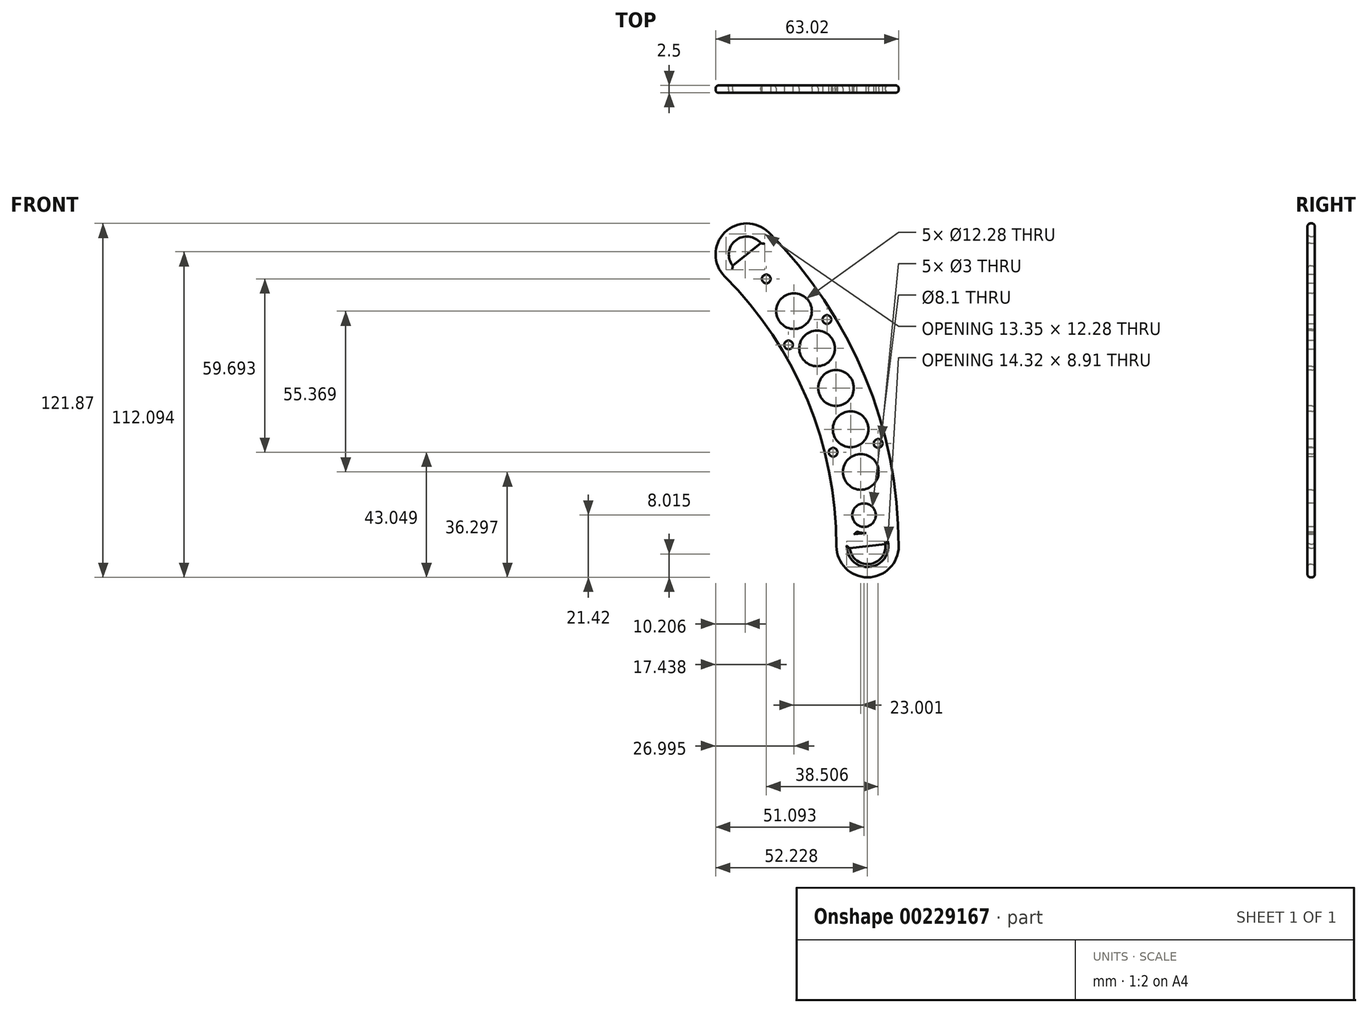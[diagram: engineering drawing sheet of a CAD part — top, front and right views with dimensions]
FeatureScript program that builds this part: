
annotation { "Feature Type Name" : "Feature", "Feature Type Description" : "" }
export const myFeature = defineFeature(function(context is Context, id is Id, definition is map)
    precondition{}
    {
        {
            var Q0;
            Q0=qCreatedBy(makeId("Front.planeOp"),FACE);
            var sketch = newSketch(context, id + "F0", { "sketchPlane" : qUnion([Q0])});
            skCircle(sketch, "E0", {"center": v(0, 0) * mm, "radius": 152.8 * mm});
            skCircle(sketch, "E1", {"center": v(0, 0) * mm, "radius": 131.4 * mm});
            skLineSegment(sketch, "E2", {"start": v(0, 0) * mm, "end": v(152.8, 0) * mm, "construction": true});
            skLineSegment(sketch, "E3", {"start": v(0, 0) * mm, "end": v(108.04, 108.04) * mm, "construction": true});
            skPoint(sketch, "E4", {"position": v(92.9, 92.9) * mm});
            skPoint(sketch, "E5", {"position": v(108.04, 108.04) * mm});
            skPoint(sketch, "E6", {"position": v(131.4, 0) * mm});
            skPoint(sketch, "E7", {"position": v(152.8, 0) * mm});
            skCircle(sketch, "E8", {"center": v(100.47, 100.47) * mm, "radius": 10.7 * mm});
            skCircle(sketch, "E9", {"center": v(142.1, 0) * mm, "radius": 10.7 * mm});
            skLineSegment(sketch, "E10", {"start": v(142.1, 0) * mm, "end": v(148.23, 0.7) * mm});
            skLineSegment(sketch, "E11", {"start": v(142.1, 0) * mm, "end": v(135.94, -0.7) * mm});
            skLineSegment(sketch, "E12", {"start": v(148.23, 0.7) * mm, "end": v(144.58, 32.71) * mm});
            skLineSegment(sketch, "E13", {"start": v(135.94, -0.7) * mm, "end": v(132.3, 31.31) * mm});
            skLineSegment(sketch, "E14", {"start": v(132.3, 31.31) * mm, "end": v(144.58, 32.71) * mm});
            skLineSegment(sketch, "E15", {"start": v(100.47, 100.47) * mm, "end": v(105.3, 104.33) * mm});
            skLineSegment(sketch, "E16", {"start": v(100.47, 100.47) * mm, "end": v(95.64, 96.62) * mm});
            skLineSegment(sketch, "E17", {"start": v(120.53, 75.25) * mm, "end": v(125.41, 79.16) * mm});
            skLineSegment(sketch, "E18", {"start": v(120.53, 75.25) * mm, "end": v(115.75, 71.44) * mm});
            skLineSegment(sketch, "E19", {"start": v(105.3, 104.33) * mm, "end": v(125.41, 79.16) * mm});
            skLineSegment(sketch, "E20", {"start": v(95.64, 96.62) * mm, "end": v(115.75, 71.44) * mm});
            skLineSegment(sketch, "E21", {"start": v(135.42, 3.88) * mm, "end": v(147.7, 5.28) * mm});
            skLineSegment(sketch, "E22", {"start": v(132.82, 26.73) * mm, "end": v(145.1, 28.13) * mm});
            skLineSegment(sketch, "E23", {"start": v(112.88, 75.04) * mm, "end": v(122.53, 82.76) * mm});
            skLineSegment(sketch, "E24", {"start": v(98.52, 93.01) * mm, "end": v(108.18, 100.73) * mm});
            skCircle(sketch, "E25", {"center": v(0, 0) * mm, "radius": 148.23 * mm, "construction": true});
            skCircle(sketch, "E26", {"center": v(0, 0) * mm, "radius": 135.95 * mm, "construction": true});
            skCircle(sketch, "E27", {"center": v(141.82, 2.29) * mm, "radius": 1 * mm});
            skCircle(sketch, "E28", {"center": v(138.7, 29.72) * mm, "radius": 1 * mm});
            skCircle(sketch, "E29", {"center": v(140.86, 10.72) * mm, "radius": 6.18 * mm});
            skLineSegment(sketch, "E30", {"start": v(122.53, 82.76) * mm, "end": v(115.75, 71.44) * mm, "construction": true});
            skLineSegment(sketch, "E31", {"start": v(112.88, 75.04) * mm, "end": v(125.41, 79.16) * mm, "construction": true});
            skCircle(sketch, "E32", {"center": v(101.91, 98.67) * mm, "radius": 1 * mm});
            skCircle(sketch, "E33", {"center": v(119.14, 77.1) * mm, "radius": 1 * mm});
            skCircle(sketch, "E34", {"center": v(107.2, 92.04) * mm, "radius": 6.18 * mm});
            skLineSegment(sketch, "E35", {"start": v(132.82, 26.73) * mm, "end": v(144.58, 32.71) * mm, "construction": true});
            skLineSegment(sketch, "E36", {"start": v(145.1, 28.13) * mm, "end": v(132.3, 31.31) * mm, "construction": true});
            skCircle(sketch, "E37", {"center": v(100.47, 100.47) * mm, "radius": 6.18 * mm});
            skCircle(sketch, "E38", {"center": v(142.1, 0) * mm, "radius": 6.19 * mm});
            skLineSegment(sketch, "E39", {"start": v(135.42, 3.88) * mm, "end": v(148.23, 0.7) * mm, "construction": true});
            skLineSegment(sketch, "E40", {"start": v(135.94, -0.7) * mm, "end": v(147.7, 5.28) * mm, "construction": true});
            skLineSegment(sketch, "E41", {"start": v(148.23, 0.7) * mm, "end": v(148.24, 0.7) * mm});
            skSolve(sketch);
        }
        {
            var Q0;
            {var subQ16=sQuery(id+"F0.wireOp",EDGE,"E18");Q0=makeQuery(id+"F0.imprint","IMPRINT",FACE,{"disambiguationData":[TD([[makeQuery(id+"F0.imprint","IMPRINT",EDGE,{"derivedFrom":subQ16}),1.0]])]});}
            var Q1;
            {var subQ14=sQuery(id+"F0.wireOp",EDGE,"E17");Q1=makeQuery(id+"F0.imprint","IMPRINT",FACE,{"disambiguationData":[TD([[makeQuery(id+"F0.imprint","IMPRINT",EDGE,{"derivedFrom":subQ14}),-1.0]])]});}
            var Q2;
            {var subQ3=sQuery(id+"F0.wireOp",EDGE,"oQQra7B9-EMDj-B2YQ-GpEd-beqhVWcHA2Qh");var subQ5=sQuery(id+"F0.wireOp",EDGE,"E22");var subQ9=makeQuery(id+"F0.imprint","INTERSECT",VERTEX,{"derivedFrom":[subQ3,subQ5]});Q2=makeQuery(id+"F0.imprint","IMPRINT",FACE,{"disambiguationData":[TD([[makeQuery(id+"F0.imprint","IMPRINT",EDGE,{"disambiguationData":[TD([[subQ9,-1.0]])],"derivedFrom":subQ3}),-1.0]])]});}
            var Q3;
            {var subQ3=sQuery(id+"F0.wireOp",EDGE,"oQQra7B9-EMDj-B2YQ-GpEd-beqhVWcHA2Qh");var subQ5=sQuery(id+"F0.wireOp",EDGE,"E22");var subQ9=makeQuery(id+"F0.imprint","INTERSECT",VERTEX,{"derivedFrom":[subQ3,subQ5]});Q3=makeQuery(id+"F0.imprint","IMPRINT",FACE,{"disambiguationData":[TD([[makeQuery(id+"F0.imprint","IMPRINT",EDGE,{"disambiguationData":[TD([[subQ9,-1.0]])],"derivedFrom":subQ3}),1.0]])]});}
            var Q4;
            {var subQ5=sQuery(id+"F0.wireOp",EDGE,"E9");var subQ8=makeQuery(id+"F0.imprint","INTERSECT",VERTEX,{"derivedFrom":[sQuery(id+"F0.wireOp",EDGE,"E1"),subQ5]});Q4=makeQuery(id+"F0.imprint","IMPRINT",FACE,{"disambiguationData":[TD([[makeQuery(id+"F0.imprint","IMPRINT",EDGE,{"disambiguationData":[TD([[subQ8,1.0]])],"derivedFrom":subQ5}),1.0]])]});}
            var Q5;
            {var subQ1=sQuery(id+"F0.wireOp",EDGE,"E9");var subQ5=makeQuery(id+"F0.imprint","INTERSECT",VERTEX,{"derivedFrom":[sQuery(id+"F0.wireOp",EDGE,"E0"),subQ1]});Q5=makeQuery(id+"F0.imprint","IMPRINT",FACE,{"disambiguationData":[TD([[makeQuery(id+"F0.imprint","IMPRINT",EDGE,{"disambiguationData":[TD([[subQ5,-1.0]])],"derivedFrom":subQ1}),1.0]])]});}
            var Q6;
            {var subQ1=sQuery(id+"F0.wireOp",EDGE,"E13");var subQ3=sQuery(id+"F0.wireOp",EDGE,"E21");var subQ4=makeQuery(id+"F0.imprint","INTERSECT",VERTEX,{"derivedFrom":[subQ1,subQ3]});Q6=makeQuery(id+"F0.imprint","IMPRINT",FACE,{"disambiguationData":[TD([[makeQuery(id+"F0.imprint","IMPRINT",EDGE,{"disambiguationData":[TD([[subQ4,-1.0]])],"derivedFrom":subQ3}),-1.0]])]});}
            var Q7;
            {var subQ1=sQuery(id+"F0.wireOp",EDGE,"E12");var subQ3=sQuery(id+"F0.wireOp",EDGE,"E21");var subQ4=makeQuery(id+"F0.imprint","INTERSECT",VERTEX,{"derivedFrom":[subQ1,subQ3]});Q7=makeQuery(id+"F0.imprint","IMPRINT",FACE,{"disambiguationData":[TD([[makeQuery(id+"F0.imprint","IMPRINT",EDGE,{"disambiguationData":[TD([[subQ4,1.0]])],"derivedFrom":subQ3}),-1.0]])]});}
            var Q8;
            {var subQ4=sQuery(id+"F0.wireOp",EDGE,"E8");var subQ5=makeQuery(id+"F0.imprint","INTERSECT",VERTEX,{"derivedFrom":[sQuery(id+"F0.wireOp",EDGE,"E0"),subQ4]});Q8=makeQuery(id+"F0.imprint","IMPRINT",FACE,{"disambiguationData":[TD([[makeQuery(id+"F0.imprint","IMPRINT",EDGE,{"disambiguationData":[TD([[subQ5,-1.0]])],"derivedFrom":subQ4}),1.0]])]});}
            var Q9;
            {var subQ5=sQuery(id+"F0.wireOp",EDGE,"E8");var subQ9=makeQuery(id+"F0.imprint","INTERSECT",VERTEX,{"derivedFrom":[sQuery(id+"F0.wireOp",EDGE,"E1"),subQ5]});Q9=makeQuery(id+"F0.imprint","IMPRINT",FACE,{"disambiguationData":[TD([[makeQuery(id+"F0.imprint","IMPRINT",EDGE,{"disambiguationData":[TD([[subQ9,1.0]])],"derivedFrom":subQ5}),1.0]])]});}
            var Q10;
            {var subQ1=sQuery(id+"F0.wireOp",EDGE,"E20");var subQ3=sQuery(id+"F0.wireOp",EDGE,"E24");var subQ4=makeQuery(id+"F0.imprint","INTERSECT",VERTEX,{"derivedFrom":[subQ1,subQ3]});Q10=makeQuery(id+"F0.imprint","IMPRINT",FACE,{"disambiguationData":[TD([[makeQuery(id+"F0.imprint","IMPRINT",EDGE,{"disambiguationData":[TD([[subQ4,-1.0]])],"derivedFrom":subQ3}),1.0]])]});}
            var Q11;
            {var subQ4=sQuery(id+"F0.wireOp",EDGE,"E16");Q11=makeQuery(id+"F0.imprint","IMPRINT",FACE,{"disambiguationData":[TD([[makeQuery(id+"F0.imprint","IMPRINT",EDGE,{"derivedFrom":subQ4}),1.0]])]});}
            var Q12;
            {var subQ0=sQuery(id+"F0.wireOp",EDGE,"E15");Q12=makeQuery(id+"F0.imprint","IMPRINT",FACE,{"disambiguationData":[TD([[makeQuery(id+"F0.imprint","IMPRINT",EDGE,{"derivedFrom":subQ0}),-1.0]])]});}
            var Q13;
            {var subQ1=sQuery(id+"F0.wireOp",EDGE,"E19");var subQ3=sQuery(id+"F0.wireOp",EDGE,"E24");var subQ4=makeQuery(id+"F0.imprint","INTERSECT",VERTEX,{"derivedFrom":[subQ1,subQ3]});Q13=makeQuery(id+"F0.imprint","IMPRINT",FACE,{"disambiguationData":[TD([[makeQuery(id+"F0.imprint","IMPRINT",EDGE,{"disambiguationData":[TD([[subQ4,1.0]])],"derivedFrom":subQ3}),1.0]])]});}
            var Q14;
            {var subQ1=sQuery(id+"F0.wireOp",EDGE,"E18");Q14=makeQuery(id+"F0.imprint","IMPRINT",FACE,{"disambiguationData":[TD([[makeQuery(id+"F0.imprint","IMPRINT",EDGE,{"derivedFrom":subQ1}),-1.0]])]});}
            var Q15;
            {var subQ1=sQuery(id+"F0.wireOp",EDGE,"E17");Q15=makeQuery(id+"F0.imprint","IMPRINT",FACE,{"disambiguationData":[TD([[makeQuery(id+"F0.imprint","IMPRINT",EDGE,{"derivedFrom":subQ1}),1.0]])]});}
            var Q16;
            {var subQ0=sQuery(id+"F0.wireOp",EDGE,"E14");Q16=makeQuery(id+"F0.imprint","IMPRINT",FACE,{"disambiguationData":[TD([[makeQuery(id+"F0.imprint","IMPRINT",EDGE,{"derivedFrom":subQ0}),-1.0]])]});}
            var Q17;
            {var subQ5=sQuery(id+"F0.wireOp",EDGE,"E10");Q17=makeQuery(id+"F0.imprint","IMPRINT",FACE,{"disambiguationData":[TD([[makeQuery(id+"F0.imprint","IMPRINT",EDGE,{"derivedFrom":subQ5}),1.0]])]});}
            var Q18;
            Q18=makeQuery(id+"F0.imprint","IMPRINT",FACE,{"disambiguationData":[TD([[makeQuery(id+"F0.imprint","IMPRINT",EDGE,{"derivedFrom":sQuery(id+"F0.wireOp",EDGE,"E27")}),-1.0]])]});
            var Q19;
            {var subQ0=sQuery(id+"F0.wireOp",EDGE,"E41");Q19=makeQuery(id+"F0.imprint","IMPRINT",FACE,{"disambiguationData":[TD([[makeQuery(id+"F0.imprint","IMPRINT",EDGE,{"derivedFrom":subQ0}),1.0]])]});}
            extrude(context, id + "F1", {"entities" : qUnion([Q0, Q1, Q2, Q3, Q4, Q5, Q6, Q7, Q8, Q9, Q10, Q11, Q12, Q13, Q14, Q15, Q16, Q17, Q18, Q19]), "depth" : 2.5 * mm});
        }
        {
            var Q0;
            Q0=makeQuery(id+"F1.opExtrude","CAP_FACE",FACE,{"disambiguationData":[OSD([sQuery(id+"F0.wireOp",EDGE,"E0"),sQuery(id+"F0.wireOp",EDGE,"E1"),sQuery(id+"F0.wireOp",EDGE,"E8"),sQuery(id+"F0.wireOp",EDGE,"E9"),sQuery(id+"F0.wireOp",EDGE,"E10"),sQuery(id+"F0.wireOp",EDGE,"E11"),sQuery(id+"F0.wireOp",EDGE,"E12"),sQuery(id+"F0.wireOp",EDGE,"E13"),sQuery(id+"F0.wireOp",EDGE,"E15"),sQuery(id+"F0.wireOp",EDGE,"E16"),sQuery(id+"F0.wireOp",EDGE,"E19"),sQuery(id+"F0.wireOp",EDGE,"E20"),sQuery(id+"F0.wireOp",EDGE,"E21"),sQuery(id+"F0.wireOp",EDGE,"E22"),sQuery(id+"F0.wireOp",EDGE,"E23"),sQuery(id+"F0.wireOp",EDGE,"E24"),sQuery(id+"F0.wireOp",EDGE,"E27"),sQuery(id+"F0.wireOp",EDGE,"E28"),sQuery(id+"F0.wireOp",EDGE,"E32"),sQuery(id+"F0.wireOp",EDGE,"E33"),sQuery(id+"F0.wireOp",EDGE,"E37"),sQuery(id+"F0.wireOp",EDGE,"E38")])],"isStart":false});
            var sketch = newSketch(context, id + "F2", { "sketchPlane" : qUnion([Q0])});
            skCircle(sketch, "E42", {"center": v(136.26, 40.28) * mm, "radius": 6.14 * mm});
            skCircle(sketch, "E43", {"center": v(124.7, 68.12) * mm, "radius": 6.14 * mm});
            skCircle(sketch, "E44", {"center": v(131.22, 54.5) * mm, "radius": 6.14 * mm});
            skCircle(sketch, "E45", {"center": v(0, 0) * mm, "radius": 142.1 * mm, "construction": true});
            skLineSegment(sketch, "E46", {"start": v(0, 0) * mm, "end": v(136.26, 40.28) * mm, "construction": true});
            skLineSegment(sketch, "E47", {"start": v(0, 0) * mm, "end": v(131.22, 54.5) * mm, "construction": true});
            skLineSegment(sketch, "E48", {"start": v(0, 0) * mm, "end": v(124.7, 68.12) * mm, "construction": true});
            skCircle(sketch, "E49", {"center": v(0, 0) * mm, "radius": 152.8 * mm, "construction": true});
            skCircle(sketch, "E50", {"center": v(0, 0) * mm, "radius": 131.4 * mm, "construction": true});
            skCircle(sketch, "E51", {"center": v(0, 0) * mm, "radius": 135.95 * mm, "construction": true});
            skCircle(sketch, "E52", {"center": v(0, 0) * mm, "radius": 148.23 * mm, "construction": true});
            skLineSegment(sketch, "E53", {"start": v(112.88, 75.04) * mm, "end": v(119.3, 65.18) * mm, "construction": true});
            skLineSegment(sketch, "E54", {"start": v(119.3, 65.18) * mm, "end": v(118, 79.14) * mm, "construction": true});
            skLineSegment(sketch, "E55", {"start": v(118, 79.14) * mm, "end": v(130.08, 71.07) * mm, "construction": true});
            skLineSegment(sketch, "E56", {"start": v(130.08, 71.07) * mm, "end": v(122.53, 82.76) * mm, "construction": true});
            skLineSegment(sketch, "E57", {"start": v(122.53, 82.76) * mm, "end": v(118, 79.14) * mm});
            skLineSegment(sketch, "E58", {"start": v(112.88, 75.04) * mm, "end": v(118, 79.14) * mm});
            skLineSegment(sketch, "E59", {"start": v(126.3, 76.91) * mm, "end": v(130.43, 79.57) * mm, "construction": true});
            skCircle(sketch, "E60", {"center": v(128.1, 78.07) * mm, "radius": 1 * mm});
            skLineSegment(sketch, "E61", {"start": v(130.37, 38.54) * mm, "end": v(132.82, 26.73) * mm});
            skLineSegment(sketch, "E62", {"start": v(145.1, 28.13) * mm, "end": v(142.22, 41.78) * mm});
            skLineSegment(sketch, "E63", {"start": v(131.6, 32.64) * mm, "end": v(127.49, 31.79) * mm});
            skLineSegment(sketch, "E64", {"start": v(143.66, 34.96) * mm, "end": v(148.5, 35.98) * mm});
            skCircle(sketch, "E65", {"center": v(130.21, 32.35) * mm, "radius": 1 * mm});
            skCircle(sketch, "E66", {"center": v(145.71, 35.4) * mm, "radius": 1 * mm});
            skLineSegment(sketch, "E67", {"start": v(116.1, 70.11) * mm, "end": v(112.55, 67.8) * mm, "construction": true});
            skCircle(sketch, "E68", {"center": v(114.87, 69.32) * mm, "radius": 1 * mm});
            skLineSegment(sketch, "E69", {"start": v(0, 0) * mm, "end": v(116.76, 80.97) * mm, "construction": true});
            skLineSegment(sketch, "E70", {"start": v(0, 0) * mm, "end": v(139.77, 25.6) * mm, "construction": true});
            skCircle(sketch, "E71", {"center": v(139.77, 25.6) * mm, "radius": 6.14 * mm});
            skCircle(sketch, "E72", {"center": v(116.76, 80.97) * mm, "radius": 6.14 * mm});
            skSolve(sketch);
        }
        {
            var Q0;
            Q0=makeQuery(id+"F2.imprint","IMPRINT",FACE,{"disambiguationData":[TD([[makeQuery(id+"F2.imprint","IMPRINT",EDGE,{"derivedFrom":sQuery(id+"F2.wireOp",EDGE,"E43")}),1.0]])]});
            var Q1;
            Q1=makeQuery(id+"F2.imprint","IMPRINT",FACE,{"disambiguationData":[TD([[makeQuery(id+"F2.imprint","IMPRINT",EDGE,{"derivedFrom":sQuery(id+"F2.wireOp",EDGE,"E44")}),1.0]])]});
            var Q2;
            Q2=makeQuery(id+"F2.imprint","IMPRINT",FACE,{"disambiguationData":[TD([[makeQuery(id+"F2.imprint","IMPRINT",EDGE,{"derivedFrom":sQuery(id+"F2.wireOp",EDGE,"E42")}),1.0]])]});
            var Q3;
            {var subQ0=sQuery(id+"F2.wireOp",EDGE,"E56");var subQ1=sQuery(id+"F2.wireOp",EDGE,"E43");var subQ2=makeQuery(id+"F2.imprint","INTERSECT",VERTEX,{"derivedFrom":[subQ1,subQ0]});Q3=makeQuery(id+"F2.imprint","IMPRINT",FACE,{"disambiguationData":[TD([[makeQuery(id+"F2.imprint","IMPRINT",EDGE,{"disambiguationData":[TD([[subQ2,-1.0]])],"derivedFrom":subQ1}),1.0]])]});}
            var Q4;
            {var subQ0=sQuery(id+"F2.wireOp",EDGE,"E54");var subQ1=sQuery(id+"F2.wireOp",EDGE,"E43");var subQ3=makeQuery(id+"F2.imprint","INTERSECT",VERTEX,{"derivedFrom":[subQ1,subQ0]});Q4=makeQuery(id+"F2.imprint","IMPRINT",FACE,{"disambiguationData":[TD([[makeQuery(id+"F2.imprint","IMPRINT",EDGE,{"disambiguationData":[TD([[subQ3,-1.0]])],"derivedFrom":subQ1}),1.0]])]});}
            var Q5;
            Q5=makeQuery(id+"F2.imprint","IMPRINT",FACE,{"disambiguationData":[TD([[makeQuery(id+"F2.imprint","IMPRINT",EDGE,{"derivedFrom":sQuery(id+"F2.wireOp",EDGE,"6Q9i7ZKX-M5Zn-dDvE-S5ua-DKoOSJd4rO0q")}),1.0]])]});
            var Q6;
            Q6=makeQuery(id+"F2.imprint","IMPRINT",FACE,{"disambiguationData":[TD([[makeQuery(id+"F2.imprint","IMPRINT",EDGE,{"derivedFrom":sQuery(id+"F2.wireOp",EDGE,"E60")}),1.0]])]});
            var Q7;
            Q7=makeQuery(id+"F2.imprint","IMPRINT",FACE,{"disambiguationData":[TD([[makeQuery(id+"F2.imprint","IMPRINT",EDGE,{"derivedFrom":sQuery(id+"F2.wireOp",EDGE,"E68")}),1.0]])]});
            var Q8;
            {var subQ0=sQuery(id+"F2.wireOp",EDGE,"E66");var subQ1=sQuery(id+"F2.wireOp",EDGE,"E64");var subQ2=makeQuery(id+"F2.imprint","INTERSECT",VERTEX,{"disambiguationData":[OD(0.0)],"derivedFrom":[subQ1,subQ0]});Q8=makeQuery(id+"F2.imprint","IMPRINT",FACE,{"disambiguationData":[TD([[makeQuery(id+"F2.imprint","IMPRINT",EDGE,{"disambiguationData":[TD([[subQ2,-1.0]])],"derivedFrom":subQ1}),1.0]])]});}
            var Q9;
            {var subQ0=sQuery(id+"F2.wireOp",EDGE,"E66");var subQ1=sQuery(id+"F2.wireOp",EDGE,"E64");var subQ2=makeQuery(id+"F2.imprint","INTERSECT",VERTEX,{"disambiguationData":[OD(0.0)],"derivedFrom":[subQ1,subQ0]});Q9=makeQuery(id+"F2.imprint","IMPRINT",FACE,{"disambiguationData":[TD([[makeQuery(id+"F2.imprint","IMPRINT",EDGE,{"disambiguationData":[TD([[subQ2,-1.0]])],"derivedFrom":subQ1}),-1.0]])]});}
            var Q10;
            {var subQ0=sQuery(id+"F2.wireOp",EDGE,"E65");var subQ1=sQuery(id+"F2.wireOp",EDGE,"E63");var subQ2=makeQuery(id+"F2.imprint","INTERSECT",VERTEX,{"disambiguationData":[OD(0.0)],"derivedFrom":[subQ1,subQ0]});Q10=makeQuery(id+"F2.imprint","IMPRINT",FACE,{"disambiguationData":[TD([[makeQuery(id+"F2.imprint","IMPRINT",EDGE,{"disambiguationData":[TD([[subQ2,-1.0]])],"derivedFrom":subQ1}),1.0]])]});}
            var Q11;
            {var subQ0=sQuery(id+"F2.wireOp",EDGE,"E65");var subQ1=sQuery(id+"F2.wireOp",EDGE,"E63");var subQ2=makeQuery(id+"F2.imprint","INTERSECT",VERTEX,{"disambiguationData":[OD(0.0)],"derivedFrom":[subQ1,subQ0]});Q11=makeQuery(id+"F2.imprint","IMPRINT",FACE,{"disambiguationData":[TD([[makeQuery(id+"F2.imprint","IMPRINT",EDGE,{"disambiguationData":[TD([[subQ2,-1.0]])],"derivedFrom":subQ1}),-1.0]])]});}
            extrude(context, id + "F3", {"entities" : qUnion([Q0, Q1, Q2, Q3, Q4, Q5, Q6, Q7, Q8, Q9, Q10, Q11]), "operationType" : NewBodyOperationType.REMOVE, "oppositeDirection" : true, "depth" : 25 * mm});
        }
        {
            var Q0;
            {var subQ1=sQuery(id+"F0.wireOp",EDGE,"E9");var subQ6=sQuery(id+"F0.wireOp",EDGE,"E12");var subQ8=makeQuery(id+"F0.imprint","INTERSECT",VERTEX,{"derivedFrom":[subQ1,subQ6]});Q0=makeQuery(id+"F0.imprint","IMPRINT",FACE,{"disambiguationData":[TD([[makeQuery(id+"F0.imprint","IMPRINT",EDGE,{"disambiguationData":[TD([[subQ8,-1.0]])],"derivedFrom":subQ1}),1.0]])]});}
            var Q1;
            {var subQ0=sQuery(id+"F0.wireOp",EDGE,"E29");var subQ1=sQuery(id+"F0.wireOp",EDGE,"E9");var subQ2=makeQuery(id+"F0.imprint","INTERSECT",VERTEX,{"disambiguationData":[OD(0.0)],"derivedFrom":[subQ1,subQ0]});Q1=makeQuery(id+"F0.imprint","IMPRINT",FACE,{"disambiguationData":[TD([[makeQuery(id+"F0.imprint","IMPRINT",EDGE,{"disambiguationData":[TD([[subQ2,-1.0]])],"derivedFrom":subQ1}),-1.0]])]});}
            var Q2;
            {var subQ0=sQuery(id+"F0.wireOp",EDGE,"E29");var subQ1=sQuery(id+"F0.wireOp",EDGE,"E9");var subQ2=makeQuery(id+"F0.imprint","INTERSECT",VERTEX,{"disambiguationData":[OD(0.0)],"derivedFrom":[subQ1,subQ0]});Q2=makeQuery(id+"F0.imprint","IMPRINT",FACE,{"disambiguationData":[TD([[makeQuery(id+"F0.imprint","IMPRINT",EDGE,{"disambiguationData":[TD([[subQ2,-1.0]])],"derivedFrom":subQ1}),1.0]])]});}
            var Q3;
            {var subQ0=sQuery(id+"F0.wireOp",EDGE,"E29");var subQ1=makeQuery(id+"F0.imprint","INTERSECT",VERTEX,{"derivedFrom":[sQuery(id+"F0.wireOp",EDGE,"E21"),subQ0]});Q3=makeQuery(id+"F0.imprint","IMPRINT",FACE,{"disambiguationData":[TD([[makeQuery(id+"F0.imprint","IMPRINT",EDGE,{"disambiguationData":[TD([[subQ1,1.0]])],"derivedFrom":subQ0}),1.0]])]});}
            var Q4;
            {var subQ0=sQuery(id+"F0.wireOp",EDGE,"E29");var subQ1=sQuery(id+"F0.wireOp",EDGE,"E9");var subQ2=makeQuery(id+"F0.imprint","INTERSECT",VERTEX,{"disambiguationData":[OD(1.0)],"derivedFrom":[subQ1,subQ0]});Q4=makeQuery(id+"F0.imprint","IMPRINT",FACE,{"disambiguationData":[TD([[makeQuery(id+"F0.imprint","IMPRINT",EDGE,{"disambiguationData":[TD([[subQ2,-1.0]])],"derivedFrom":subQ1}),1.0]])]});}
            var Q5;
            {var subQ0=sQuery(id+"F0.wireOp",EDGE,"E38");var subQ1=sQuery(id+"F0.wireOp",EDGE,"E21");var subQ2=makeQuery(id+"F0.imprint","INTERSECT",VERTEX,{"disambiguationData":[OD(0.0)],"derivedFrom":[subQ1,subQ0]});Q5=makeQuery(id+"F0.imprint","IMPRINT",FACE,{"disambiguationData":[TD([[makeQuery(id+"F0.imprint","IMPRINT",EDGE,{"disambiguationData":[TD([[subQ2,-1.0]])],"derivedFrom":subQ1}),1.0]])]});}
            var Q6;
            {var subQ0=sQuery(id+"F0.wireOp",EDGE,"E29");var subQ1=sQuery(id+"F0.wireOp",EDGE,"E21");var subQ2=makeQuery(id+"F0.imprint","INTERSECT",VERTEX,{"derivedFrom":[subQ1,subQ0]});Q6=makeQuery(id+"F0.imprint","IMPRINT",FACE,{"disambiguationData":[TD([[makeQuery(id+"F0.imprint","IMPRINT",EDGE,{"disambiguationData":[TD([[subQ2,-1.0]])],"derivedFrom":subQ1}),1.0]])]});}
            var Q7;
            {var subQ0=sQuery(id+"F0.wireOp",EDGE,"E22");Q7=makeQuery(id+"F0.imprint","IMPRINT",FACE,{"disambiguationData":[TD([[makeQuery(id+"F0.imprint","IMPRINT",EDGE,{"derivedFrom":subQ0}),-1.0]])]});}
            var Q8;
            {var subQ0=sQuery(id+"F0.wireOp",EDGE,"E12");var subQ1=sQuery(id+"F0.wireOp",EDGE,"E9");var subQ2=makeQuery(id+"F0.imprint","INTERSECT",VERTEX,{"derivedFrom":[subQ1,subQ0]});Q8=makeQuery(id+"F0.imprint","IMPRINT",FACE,{"disambiguationData":[TD([[makeQuery(id+"F0.imprint","IMPRINT",EDGE,{"disambiguationData":[TD([[subQ2,-1.0]])],"derivedFrom":subQ1}),-1.0]])]});}
            var Q9;
            {var subQ0=sQuery(id+"F0.wireOp",EDGE,"E29");var subQ1=sQuery(id+"F0.wireOp",EDGE,"E9");var subQ2=makeQuery(id+"F0.imprint","INTERSECT",VERTEX,{"disambiguationData":[OD(1.0)],"derivedFrom":[subQ1,subQ0]});Q9=makeQuery(id+"F0.imprint","IMPRINT",FACE,{"disambiguationData":[TD([[makeQuery(id+"F0.imprint","IMPRINT",EDGE,{"disambiguationData":[TD([[subQ2,-1.0]])],"derivedFrom":subQ1}),-1.0]])]});}
            var Q10;
            {var subQ0=sQuery(id+"F0.wireOp",EDGE,"E23");Q10=makeQuery(id+"F0.imprint","IMPRINT",FACE,{"disambiguationData":[TD([[makeQuery(id+"F0.imprint","IMPRINT",EDGE,{"derivedFrom":subQ0}),1.0]])]});}
            var Q11;
            {var subQ0=sQuery(id+"F0.wireOp",EDGE,"E34");var subQ1=sQuery(id+"F0.wireOp",EDGE,"E8");var subQ2=makeQuery(id+"F0.imprint","INTERSECT",VERTEX,{"disambiguationData":[OD(0.0)],"derivedFrom":[subQ1,subQ0]});Q11=makeQuery(id+"F0.imprint","IMPRINT",FACE,{"disambiguationData":[TD([[makeQuery(id+"F0.imprint","IMPRINT",EDGE,{"disambiguationData":[TD([[subQ2,-1.0]])],"derivedFrom":subQ1}),-1.0]])]});}
            var Q12;
            {var subQ0=sQuery(id+"F0.wireOp",EDGE,"E34");var subQ1=sQuery(id+"F0.wireOp",EDGE,"E8");var subQ2=makeQuery(id+"F0.imprint","INTERSECT",VERTEX,{"disambiguationData":[OD(0.0)],"derivedFrom":[subQ1,subQ0]});Q12=makeQuery(id+"F0.imprint","IMPRINT",FACE,{"disambiguationData":[TD([[makeQuery(id+"F0.imprint","IMPRINT",EDGE,{"disambiguationData":[TD([[subQ2,-1.0]])],"derivedFrom":subQ1}),1.0]])]});}
            var Q13;
            {var subQ0=sQuery(id+"F0.wireOp",EDGE,"E34");var subQ1=sQuery(id+"F0.wireOp",EDGE,"E8");var subQ2=makeQuery(id+"F0.imprint","INTERSECT",VERTEX,{"disambiguationData":[OD(1.0)],"derivedFrom":[subQ1,subQ0]});Q13=makeQuery(id+"F0.imprint","IMPRINT",FACE,{"disambiguationData":[TD([[makeQuery(id+"F0.imprint","IMPRINT",EDGE,{"disambiguationData":[TD([[subQ2,-1.0]])],"derivedFrom":subQ1}),1.0]])]});}
            var Q14;
            {var subQ0=sQuery(id+"F0.wireOp",EDGE,"E34");var subQ1=sQuery(id+"F0.wireOp",EDGE,"E24");var subQ2=makeQuery(id+"F0.imprint","INTERSECT",VERTEX,{"derivedFrom":[subQ1,subQ0]});Q14=makeQuery(id+"F0.imprint","IMPRINT",FACE,{"disambiguationData":[TD([[makeQuery(id+"F0.imprint","IMPRINT",EDGE,{"disambiguationData":[TD([[subQ2,-1.0]])],"derivedFrom":subQ1}),-1.0]])]});}
            var Q15;
            {var subQ0=sQuery(id+"F0.wireOp",EDGE,"E34");var subQ1=makeQuery(id+"F0.imprint","INTERSECT",VERTEX,{"derivedFrom":[sQuery(id+"F0.wireOp",EDGE,"E24"),subQ0]});Q15=makeQuery(id+"F0.imprint","IMPRINT",FACE,{"disambiguationData":[TD([[makeQuery(id+"F0.imprint","IMPRINT",EDGE,{"disambiguationData":[TD([[subQ1,1.0]])],"derivedFrom":subQ0}),1.0]])]});}
            var Q16;
            {var subQ0=sQuery(id+"F0.wireOp",EDGE,"E37");var subQ1=sQuery(id+"F0.wireOp",EDGE,"E24");var subQ2=makeQuery(id+"F0.imprint","INTERSECT",VERTEX,{"disambiguationData":[OD(0.0)],"derivedFrom":[subQ1,subQ0]});Q16=makeQuery(id+"F0.imprint","IMPRINT",FACE,{"disambiguationData":[TD([[makeQuery(id+"F0.imprint","IMPRINT",EDGE,{"disambiguationData":[TD([[subQ2,-1.0]])],"derivedFrom":subQ1}),-1.0]])]});}
            var Q17;
            {var subQ1=sQuery(id+"F0.wireOp",EDGE,"E8");var subQ6=sQuery(id+"F0.wireOp",EDGE,"E20");var subQ9=makeQuery(id+"F0.imprint","INTERSECT",VERTEX,{"derivedFrom":[subQ1,subQ6]});Q17=makeQuery(id+"F0.imprint","IMPRINT",FACE,{"disambiguationData":[TD([[makeQuery(id+"F0.imprint","IMPRINT",EDGE,{"disambiguationData":[TD([[subQ9,-1.0]])],"derivedFrom":subQ1}),1.0]])]});}
            var Q18;
            {var subQ0=sQuery(id+"F0.wireOp",EDGE,"E34");var subQ1=sQuery(id+"F0.wireOp",EDGE,"E8");var subQ2=makeQuery(id+"F0.imprint","INTERSECT",VERTEX,{"disambiguationData":[OD(1.0)],"derivedFrom":[subQ1,subQ0]});Q18=makeQuery(id+"F0.imprint","IMPRINT",FACE,{"disambiguationData":[TD([[makeQuery(id+"F0.imprint","IMPRINT",EDGE,{"disambiguationData":[TD([[subQ2,-1.0]])],"derivedFrom":subQ1}),-1.0]])]});}
            var Q19;
            {var subQ0=sQuery(id+"F0.wireOp",EDGE,"E20");var subQ1=sQuery(id+"F0.wireOp",EDGE,"E8");var subQ2=makeQuery(id+"F0.imprint","INTERSECT",VERTEX,{"derivedFrom":[subQ1,subQ0]});Q19=makeQuery(id+"F0.imprint","IMPRINT",FACE,{"disambiguationData":[TD([[makeQuery(id+"F0.imprint","IMPRINT",EDGE,{"disambiguationData":[TD([[subQ2,-1.0]])],"derivedFrom":subQ1}),-1.0]])]});}
            extrude(context, id + "F4", {"entities" : qUnion([Q0, Q1, Q2, Q3, Q4, Q5, Q6, Q7, Q8, Q9, Q10, Q11, Q12, Q13, Q14, Q15, Q16, Q17, Q18, Q19]), "operationType" : NewBodyOperationType.ADD, "depth" : 2.5 * mm});
        }
        {
            var Q0;
            {var subQ0=sQuery(id+"F0.wireOp",EDGE,"E24");var subQ1=sQuery(id+"F0.wireOp",EDGE,"E23");var subQ2=sQuery(id+"F0.wireOp",EDGE,"E20");var subQ3=sQuery(id+"F0.wireOp",EDGE,"E19");var subQ4=sQuery(id+"F0.wireOp",EDGE,"E22");var subQ5=sQuery(id+"F0.wireOp",EDGE,"E21");var subQ6=sQuery(id+"F0.wireOp",EDGE,"E13");var subQ7=sQuery(id+"F0.wireOp",EDGE,"E12");Q0=makeQuery(id+"F4.boolean.opBoolean","MERGE",FACE,{"derivedFrom":[makeQuery(id+"F1.opExtrude","CAP_FACE",FACE,{"disambiguationData":[OSD([sQuery(id+"F0.wireOp",EDGE,"E0"),sQuery(id+"F0.wireOp",EDGE,"E1"),sQuery(id+"F0.wireOp",EDGE,"E8"),sQuery(id+"F0.wireOp",EDGE,"E9"),sQuery(id+"F0.wireOp",EDGE,"E10"),sQuery(id+"F0.wireOp",EDGE,"E11"),subQ7,subQ6,sQuery(id+"F0.wireOp",EDGE,"E15"),sQuery(id+"F0.wireOp",EDGE,"E16"),subQ3,subQ2,subQ5,subQ4,subQ1,subQ0,sQuery(id+"F0.wireOp",EDGE,"E27"),sQuery(id+"F0.wireOp",EDGE,"E28"),sQuery(id+"F0.wireOp",EDGE,"E32"),sQuery(id+"F0.wireOp",EDGE,"E33"),sQuery(id+"F0.wireOp",EDGE,"E37"),sQuery(id+"F0.wireOp",EDGE,"E38")])],"isStart":false}),makeQuery(id+"F4.opExtrude","CAP_FACE",FACE,{"disambiguationData":[OSD([subQ7,subQ6,subQ5,subQ4])],"isStart":false}),makeQuery(id+"F4.opExtrude","CAP_FACE",FACE,{"disambiguationData":[OSD([subQ3,subQ2,subQ1,subQ0])],"isStart":false})]});}
            var sketch = newSketch(context, id + "F5", { "sketchPlane" : qUnion([Q0])});
            skCircle(sketch, "E73", {"center": v(140.86, 10.72) * mm, "radius": 4.05 * mm});
            skCircle(sketch, "E74", {"center": v(107.2, 92.04) * mm, "radius": 4.05 * mm});
            skSolve(sketch);
        }
        {
            var Q0;
            Q0 = qSketchRegion(id + "F5", true);
            extrude(context, id + "F6", {"entities" : qUnion([Q0]), "operationType" : NewBodyOperationType.REMOVE, "oppositeDirection" : true, "depth" : 25 * mm});
        }
        {
            var Q0;
            Q0=makeQuery(id+"F0.imprint","IMPRINT",FACE,{"disambiguationData":[TD([[makeQuery(id+"F0.imprint","IMPRINT",EDGE,{"derivedFrom":sQuery(id+"F0.wireOp",EDGE,"E32")}),1.0]])]});
            var Q1;
            Q1=makeQuery(id+"F0.imprint","IMPRINT",FACE,{"disambiguationData":[TD([[makeQuery(id+"F0.imprint","IMPRINT",EDGE,{"derivedFrom":sQuery(id+"F0.wireOp",EDGE,"E33")}),1.0]])]});
            var Q2;
            Q2=makeQuery(id+"F0.imprint","IMPRINT",FACE,{"disambiguationData":[TD([[makeQuery(id+"F0.imprint","IMPRINT",EDGE,{"derivedFrom":sQuery(id+"F0.wireOp",EDGE,"E28")}),1.0]])]});
            var Q3;
            Q3=makeQuery(id+"F0.imprint","IMPRINT",FACE,{"disambiguationData":[TD([[makeQuery(id+"F0.imprint","IMPRINT",EDGE,{"derivedFrom":sQuery(id+"F0.wireOp",EDGE,"E27")}),1.0]])]});
            extrude(context, id + "F7", {"entities" : qUnion([Q0, Q1, Q2, Q3]), "operationType" : NewBodyOperationType.ADD, "depth" : 2.5 * mm});
        }
        {
            var Q0;
            {var subQ0=sQuery(id+"F2.wireOp",EDGE,"E71");var subQ1=makeQuery(id+"F1.opExtrude","CAP_EDGE",EDGE,{"disambiguationData":[OSD([sQuery(id+"F0.wireOp",EDGE,"E22")])],"isStart":false});var subQ2=makeQuery(id+"F2.imprint","INTERSECT",VERTEX,{"derivedFrom":[subQ1,subQ0]});Q0=makeQuery(id+"F2.imprint","IMPRINT",FACE,{"disambiguationData":[TD([[makeQuery(id+"F2.imprint","IMPRINT",EDGE,{"disambiguationData":[TD([[subQ2,-1.0]])],"derivedFrom":subQ0}),1.0]])]});}
            var Q1;
            Q1=makeQuery(id+"F2.imprint","IMPRINT",FACE,{"disambiguationData":[TD([[makeQuery(id+"F2.imprint","IMPRINT",EDGE,{"derivedFrom":makeQuery(id+"F1.opExtrude","CAP_EDGE",EDGE,{"disambiguationData":[OSD([sQuery(id+"F0.wireOp",EDGE,"E28")])],"isStart":false})}),-1.0]])]});
            var Q2;
            Q2=makeQuery(id+"F2.imprint","IMPRINT",FACE,{"disambiguationData":[TD([[makeQuery(id+"F2.imprint","IMPRINT",EDGE,{"derivedFrom":makeQuery(id+"F1.opExtrude","CAP_EDGE",EDGE,{"disambiguationData":[OSD([sQuery(id+"F0.wireOp",EDGE,"E28")])],"isStart":false})}),1.0]])]});
            var Q3;
            {var subQ0=sQuery(id+"F2.wireOp",EDGE,"E62");var subQ3=sQuery(id+"F2.wireOp",EDGE,"E71");var subQ4=makeQuery(id+"F2.imprint","INTERSECT",VERTEX,{"derivedFrom":[subQ0,subQ3]});Q3=makeQuery(id+"F2.imprint","IMPRINT",FACE,{"disambiguationData":[TD([[makeQuery(id+"F2.imprint","IMPRINT",EDGE,{"disambiguationData":[TD([[subQ4,1.0]])],"derivedFrom":subQ3}),1.0]])]});}
            var Q4;
            {var subQ0=sQuery(id+"F2.wireOp",EDGE,"E57");Q4=makeQuery(id+"F2.imprint","IMPRINT",FACE,{"disambiguationData":[TD([[makeQuery(id+"F2.imprint","IMPRINT",EDGE,{"derivedFrom":subQ0}),1.0]])]});}
            var Q5;
            {var subQ5=sQuery(id+"F2.wireOp",EDGE,"E57");Q5=makeQuery(id+"F2.imprint","IMPRINT",FACE,{"disambiguationData":[TD([[makeQuery(id+"F2.imprint","IMPRINT",EDGE,{"derivedFrom":subQ5}),-1.0]])]});}
            var Q6;
            Q6=makeQuery(id+"F2.imprint","IMPRINT",FACE,{"disambiguationData":[TD([[makeQuery(id+"F2.imprint","IMPRINT",EDGE,{"derivedFrom":makeQuery(id+"F1.opExtrude","CAP_EDGE",EDGE,{"disambiguationData":[OSD([sQuery(id+"F0.wireOp",EDGE,"E33")])],"isStart":false})}),1.0]])]});
            extrude(context, id + "F8", {"entities" : qUnion([Q0, Q1, Q2, Q3, Q4, Q5, Q6]), "operationType" : NewBodyOperationType.REMOVE, "oppositeDirection" : true, "depth" : 25 * mm});
        }
        {
            var Q0;
            Q0=makeQuery(id+"F8.boolean.opBoolean","COPY",EDGE,{"derivedFrom":makeQuery(id+"F8.opExtrude","CAP_EDGE",EDGE,{"disambiguationData":[OSD([sQuery(id+"F2.wireOp",EDGE,"E72")])],"isStart":true})});
            var Q1;
            Q1=makeQuery(id+"F8.boolean.opBoolean","COPY",EDGE,{"derivedFrom":makeQuery(id+"F8.opExtrude","CAP_EDGE",EDGE,{"disambiguationData":[OSD([sQuery(id+"F2.wireOp",EDGE,"E71")])],"isStart":true})});
            var Q2;
            {var subQ0=sQuery(id+"F0.wireOp",EDGE,"E33");var subQ1=sQuery(id+"F0.wireOp",EDGE,"E32");var subQ2=sQuery(id+"F0.wireOp",EDGE,"E28");var subQ3=sQuery(id+"F0.wireOp",EDGE,"E27");var subQ4=sQuery(id+"F0.wireOp",EDGE,"E24");var subQ5=sQuery(id+"F0.wireOp",EDGE,"E23");var subQ6=sQuery(id+"F0.wireOp",EDGE,"E20");var subQ7=sQuery(id+"F0.wireOp",EDGE,"E19");var subQ8=sQuery(id+"F0.wireOp",EDGE,"E22");var subQ9=sQuery(id+"F0.wireOp",EDGE,"E21");var subQ10=sQuery(id+"F0.wireOp",EDGE,"E13");var subQ11=sQuery(id+"F0.wireOp",EDGE,"E12");Q2=makeQuery(id+"F8.boolean.opBoolean","INTERSECT",EDGE,{"derivedFrom":[makeQuery(id+"F7.boolean.opBoolean","MERGE",FACE,{"derivedFrom":[makeQuery(id+"F4.boolean.opBoolean","MERGE",FACE,{"derivedFrom":[makeQuery(id+"F1.opExtrude","CAP_FACE",FACE,{"disambiguationData":[OSD([sQuery(id+"F0.wireOp",EDGE,"E0"),sQuery(id+"F0.wireOp",EDGE,"E1"),sQuery(id+"F0.wireOp",EDGE,"E8"),sQuery(id+"F0.wireOp",EDGE,"E9"),sQuery(id+"F0.wireOp",EDGE,"E10"),sQuery(id+"F0.wireOp",EDGE,"E11"),subQ11,subQ10,sQuery(id+"F0.wireOp",EDGE,"E15"),sQuery(id+"F0.wireOp",EDGE,"E16"),subQ7,subQ6,subQ9,subQ8,subQ5,subQ4,subQ3,subQ2,subQ1,subQ0,sQuery(id+"F0.wireOp",EDGE,"E37"),sQuery(id+"F0.wireOp",EDGE,"E38")])],"isStart":true}),makeQuery(id+"F4.opExtrude","CAP_FACE",FACE,{"disambiguationData":[OSD([subQ11,subQ10,subQ9,subQ8])],"isStart":true}),makeQuery(id+"F4.opExtrude","CAP_FACE",FACE,{"disambiguationData":[OSD([subQ7,subQ6,subQ5,subQ4])],"isStart":true})]}),makeQuery(id+"F7.opExtrude","CAP_FACE",FACE,{"disambiguationData":[OSD([subQ3])],"isStart":true}),makeQuery(id+"F7.opExtrude","CAP_FACE",FACE,{"disambiguationData":[OSD([subQ2])],"isStart":true}),makeQuery(id+"F7.opExtrude","CAP_FACE",FACE,{"disambiguationData":[OSD([subQ1])],"isStart":true}),makeQuery(id+"F7.opExtrude","CAP_FACE",FACE,{"disambiguationData":[OSD([subQ0])],"isStart":true})]}),makeQuery(id+"F8.opExtrude","SWEPT_FACE",FACE,{"disambiguationData":[OSD([sQuery(id+"F2.wireOp",EDGE,"E71")])]})]});}
            var Q3;
            {var subQ0=sQuery(id+"F0.wireOp",EDGE,"E33");var subQ1=sQuery(id+"F0.wireOp",EDGE,"E32");var subQ2=sQuery(id+"F0.wireOp",EDGE,"E28");var subQ3=sQuery(id+"F0.wireOp",EDGE,"E27");var subQ4=sQuery(id+"F0.wireOp",EDGE,"E24");var subQ5=sQuery(id+"F0.wireOp",EDGE,"E23");var subQ6=sQuery(id+"F0.wireOp",EDGE,"E20");var subQ7=sQuery(id+"F0.wireOp",EDGE,"E19");var subQ8=sQuery(id+"F0.wireOp",EDGE,"E22");var subQ9=sQuery(id+"F0.wireOp",EDGE,"E21");var subQ10=sQuery(id+"F0.wireOp",EDGE,"E13");var subQ11=sQuery(id+"F0.wireOp",EDGE,"E12");Q3=makeQuery(id+"F8.boolean.opBoolean","INTERSECT",EDGE,{"derivedFrom":[makeQuery(id+"F7.boolean.opBoolean","MERGE",FACE,{"derivedFrom":[makeQuery(id+"F4.boolean.opBoolean","MERGE",FACE,{"derivedFrom":[makeQuery(id+"F1.opExtrude","CAP_FACE",FACE,{"disambiguationData":[OSD([sQuery(id+"F0.wireOp",EDGE,"E0"),sQuery(id+"F0.wireOp",EDGE,"E1"),sQuery(id+"F0.wireOp",EDGE,"E8"),sQuery(id+"F0.wireOp",EDGE,"E9"),sQuery(id+"F0.wireOp",EDGE,"E10"),sQuery(id+"F0.wireOp",EDGE,"E11"),subQ11,subQ10,sQuery(id+"F0.wireOp",EDGE,"E15"),sQuery(id+"F0.wireOp",EDGE,"E16"),subQ7,subQ6,subQ9,subQ8,subQ5,subQ4,subQ3,subQ2,subQ1,subQ0,sQuery(id+"F0.wireOp",EDGE,"E37"),sQuery(id+"F0.wireOp",EDGE,"E38")])],"isStart":true}),makeQuery(id+"F4.opExtrude","CAP_FACE",FACE,{"disambiguationData":[OSD([subQ11,subQ10,subQ9,subQ8])],"isStart":true}),makeQuery(id+"F4.opExtrude","CAP_FACE",FACE,{"disambiguationData":[OSD([subQ7,subQ6,subQ5,subQ4])],"isStart":true})]}),makeQuery(id+"F7.opExtrude","CAP_FACE",FACE,{"disambiguationData":[OSD([subQ3])],"isStart":true}),makeQuery(id+"F7.opExtrude","CAP_FACE",FACE,{"disambiguationData":[OSD([subQ2])],"isStart":true}),makeQuery(id+"F7.opExtrude","CAP_FACE",FACE,{"disambiguationData":[OSD([subQ1])],"isStart":true}),makeQuery(id+"F7.opExtrude","CAP_FACE",FACE,{"disambiguationData":[OSD([subQ0])],"isStart":true})]}),makeQuery(id+"F8.opExtrude","SWEPT_FACE",FACE,{"disambiguationData":[OSD([sQuery(id+"F2.wireOp",EDGE,"E72")])]})]});}
            fillet(context, id + "F9", {"entities" : qUnion([Q0, Q1, Q2, Q3]), "radius" : 1 * mm, "tangentPropagation" : true, "allowEdgeOverflow" : false});
        }
        {
            var Q0;
            Q0=makeQuery(id+"F2.imprint","IMPRINT",FACE,{"disambiguationData":[TD([[makeQuery(id+"F2.imprint","IMPRINT",EDGE,{"derivedFrom":sQuery(id+"F2.wireOp",EDGE,"E43")}),-1.0]])]});
            var sketch = newSketch(context, id + "F10", { "sketchPlane" : qUnion([Q0])});
            skCircle(sketch, "E75", {"center": v(130.21, 32.35) * mm, "radius": 1.5 * mm});
            skCircle(sketch, "E76", {"center": v(145.71, 35.4) * mm, "radius": 1.5 * mm});
            skCircle(sketch, "E77", {"center": v(128.1, 78.07) * mm, "radius": 1.5 * mm});
            skCircle(sketch, "E78", {"center": v(114.87, 69.32) * mm, "radius": 1.5 * mm});
            skSolve(sketch);
        }
        {
            var Q0;
            Q0 = qSketchRegion(id + "F10", true);
            extrude(context, id + "F11", {"entities" : qUnion([Q0]), "operationType" : NewBodyOperationType.REMOVE, "oppositeDirection" : true, "depth" : 25 * mm});
        }
        {
            var Q0;
            Q0=makeQuery(id+"F2.imprint","IMPRINT",FACE,{"disambiguationData":[TD([[makeQuery(id+"F2.imprint","IMPRINT",EDGE,{"derivedFrom":sQuery(id+"F2.wireOp",EDGE,"E43")}),-1.0]])]});
            var sketch = newSketch(context, id + "F12", { "sketchPlane" : qUnion([Q0])});
            skCircle(sketch, "E79", {"center": v(107.2, 92.04) * mm, "radius": 4.05 * mm});
            skCircle(sketch, "E80", {"center": v(107.2, 92.04) * mm, "radius": 1.5 * mm});
            skSolve(sketch);
        }
        {
            var Q0;
            Q0 = qSketchRegion(id + "F12", true);
            extrude(context, id + "F13", {"entities" : qUnion([Q0]), "operationType" : NewBodyOperationType.ADD, "oppositeDirection" : true, "depth" : 2.5 * mm});
        }
        {
            var Q0;
            Q0=makeQuery(id+"F1.opExtrude","CAP_EDGE",EDGE,{"disambiguationData":[OSD([sQuery(id+"F0.wireOp",EDGE,"E38")])],"isStart":false});
            var Q1;
            Q1=makeQuery(id+"F1.opExtrude","CAP_EDGE",EDGE,{"disambiguationData":[OSD([sQuery(id+"F0.wireOp",EDGE,"E10"),sQuery(id+"F0.wireOp",EDGE,"E11")])],"isStart":false});
            var Q2;
            Q2=makeQuery(id+"F1.opExtrude","CAP_EDGE",EDGE,{"disambiguationData":[OSD([sQuery(id+"F0.wireOp",EDGE,"E0")])],"isStart":false});
            var Q3;
            Q3=makeQuery(id+"F3.boolean.opBoolean","COPY",EDGE,{"derivedFrom":makeQuery(id+"F3.opExtrude","CAP_EDGE",EDGE,{"disambiguationData":[OSD([sQuery(id+"F2.wireOp",EDGE,"E42")])],"isStart":true})});
            var Q4;
            Q4=makeQuery(id+"F3.boolean.opBoolean","COPY",EDGE,{"derivedFrom":makeQuery(id+"F3.opExtrude","CAP_EDGE",EDGE,{"disambiguationData":[OSD([sQuery(id+"F2.wireOp",EDGE,"E43")])],"isStart":true})});
            var Q5;
            Q5=makeQuery(id+"F3.boolean.opBoolean","COPY",EDGE,{"derivedFrom":makeQuery(id+"F3.opExtrude","CAP_EDGE",EDGE,{"disambiguationData":[OSD([sQuery(id+"F2.wireOp",EDGE,"E44")])],"isStart":true})});
            var Q6;
            Q6=makeQuery(id+"F1.opExtrude","CAP_EDGE",EDGE,{"disambiguationData":[OSD([sQuery(id+"F0.wireOp",EDGE,"E15"),sQuery(id+"F0.wireOp",EDGE,"E16")])],"isStart":false});
            var Q7;
            Q7=makeQuery(id+"F1.opExtrude","CAP_EDGE",EDGE,{"disambiguationData":[OSD([sQuery(id+"F0.wireOp",EDGE,"E37")])],"isStart":false});
            var Q8;
            Q8=makeQuery(id+"F1.opExtrude","CAP_EDGE",EDGE,{"disambiguationData":[OSD([sQuery(id+"F0.wireOp",EDGE,"E8")])],"isStart":true});
            var Q9;
            Q9=makeQuery(id+"F1.opExtrude","CAP_EDGE",EDGE,{"disambiguationData":[OSD([sQuery(id+"F0.wireOp",EDGE,"E37")])],"isStart":true});
            var Q10;
            Q10=makeQuery(id+"F1.opExtrude","CAP_EDGE",EDGE,{"disambiguationData":[OSD([sQuery(id+"F0.wireOp",EDGE,"E15"),sQuery(id+"F0.wireOp",EDGE,"E16")])],"isStart":true});
            var Q11;
            Q11=makeQuery(id+"F1.opExtrude","CAP_EDGE",EDGE,{"disambiguationData":[OSD([sQuery(id+"F0.wireOp",EDGE,"E38")])],"isStart":true});
            var Q12;
            Q12=makeQuery(id+"F1.opExtrude","CAP_EDGE",EDGE,{"disambiguationData":[OSD([sQuery(id+"F0.wireOp",EDGE,"E10"),sQuery(id+"F0.wireOp",EDGE,"E11")])],"isStart":true});
            var Q13;
            Q13=makeQuery(id+"F3.boolean.opBoolean","INTERSECT",EDGE,{"derivedFrom":[makeQuery(id+"F1.opExtrude","CAP_FACE",FACE,{"disambiguationData":[OSD([sQuery(id+"F0.wireOp",EDGE,"E0"),sQuery(id+"F0.wireOp",EDGE,"E1"),sQuery(id+"F0.wireOp",EDGE,"E8"),sQuery(id+"F0.wireOp",EDGE,"E9"),sQuery(id+"F0.wireOp",EDGE,"E10"),sQuery(id+"F0.wireOp",EDGE,"E11"),sQuery(id+"F0.wireOp",EDGE,"E12"),sQuery(id+"F0.wireOp",EDGE,"E13"),sQuery(id+"F0.wireOp",EDGE,"E15"),sQuery(id+"F0.wireOp",EDGE,"E16"),sQuery(id+"F0.wireOp",EDGE,"E19"),sQuery(id+"F0.wireOp",EDGE,"E20"),sQuery(id+"F0.wireOp",EDGE,"E21"),sQuery(id+"F0.wireOp",EDGE,"E22"),sQuery(id+"F0.wireOp",EDGE,"E23"),sQuery(id+"F0.wireOp",EDGE,"E24"),sQuery(id+"F0.wireOp",EDGE,"E27"),sQuery(id+"F0.wireOp",EDGE,"E28"),sQuery(id+"F0.wireOp",EDGE,"E32"),sQuery(id+"F0.wireOp",EDGE,"E33"),sQuery(id+"F0.wireOp",EDGE,"E37"),sQuery(id+"F0.wireOp",EDGE,"E38"),sQuery(id+"F0.wireOp",EDGE,"E41")])],"isStart":true}),makeQuery(id+"F3.opExtrude","SWEPT_FACE",FACE,{"disambiguationData":[OSD([sQuery(id+"F2.wireOp",EDGE,"E43")])]})]});
            var Q14;
            Q14=makeQuery(id+"F3.boolean.opBoolean","INTERSECT",EDGE,{"derivedFrom":[makeQuery(id+"F1.opExtrude","CAP_FACE",FACE,{"disambiguationData":[OSD([sQuery(id+"F0.wireOp",EDGE,"E0"),sQuery(id+"F0.wireOp",EDGE,"E1"),sQuery(id+"F0.wireOp",EDGE,"E8"),sQuery(id+"F0.wireOp",EDGE,"E9"),sQuery(id+"F0.wireOp",EDGE,"E10"),sQuery(id+"F0.wireOp",EDGE,"E11"),sQuery(id+"F0.wireOp",EDGE,"E12"),sQuery(id+"F0.wireOp",EDGE,"E13"),sQuery(id+"F0.wireOp",EDGE,"E15"),sQuery(id+"F0.wireOp",EDGE,"E16"),sQuery(id+"F0.wireOp",EDGE,"E19"),sQuery(id+"F0.wireOp",EDGE,"E20"),sQuery(id+"F0.wireOp",EDGE,"E21"),sQuery(id+"F0.wireOp",EDGE,"E22"),sQuery(id+"F0.wireOp",EDGE,"E23"),sQuery(id+"F0.wireOp",EDGE,"E24"),sQuery(id+"F0.wireOp",EDGE,"E27"),sQuery(id+"F0.wireOp",EDGE,"E28"),sQuery(id+"F0.wireOp",EDGE,"E32"),sQuery(id+"F0.wireOp",EDGE,"E33"),sQuery(id+"F0.wireOp",EDGE,"E37"),sQuery(id+"F0.wireOp",EDGE,"E38"),sQuery(id+"F0.wireOp",EDGE,"E41")])],"isStart":true}),makeQuery(id+"F3.opExtrude","SWEPT_FACE",FACE,{"disambiguationData":[OSD([sQuery(id+"F2.wireOp",EDGE,"E44")])]})]});
            var Q15;
            Q15=makeQuery(id+"F3.boolean.opBoolean","INTERSECT",EDGE,{"derivedFrom":[makeQuery(id+"F1.opExtrude","CAP_FACE",FACE,{"disambiguationData":[OSD([sQuery(id+"F0.wireOp",EDGE,"E0"),sQuery(id+"F0.wireOp",EDGE,"E1"),sQuery(id+"F0.wireOp",EDGE,"E8"),sQuery(id+"F0.wireOp",EDGE,"E9"),sQuery(id+"F0.wireOp",EDGE,"E10"),sQuery(id+"F0.wireOp",EDGE,"E11"),sQuery(id+"F0.wireOp",EDGE,"E12"),sQuery(id+"F0.wireOp",EDGE,"E13"),sQuery(id+"F0.wireOp",EDGE,"E15"),sQuery(id+"F0.wireOp",EDGE,"E16"),sQuery(id+"F0.wireOp",EDGE,"E19"),sQuery(id+"F0.wireOp",EDGE,"E20"),sQuery(id+"F0.wireOp",EDGE,"E21"),sQuery(id+"F0.wireOp",EDGE,"E22"),sQuery(id+"F0.wireOp",EDGE,"E23"),sQuery(id+"F0.wireOp",EDGE,"E24"),sQuery(id+"F0.wireOp",EDGE,"E27"),sQuery(id+"F0.wireOp",EDGE,"E28"),sQuery(id+"F0.wireOp",EDGE,"E32"),sQuery(id+"F0.wireOp",EDGE,"E33"),sQuery(id+"F0.wireOp",EDGE,"E37"),sQuery(id+"F0.wireOp",EDGE,"E38"),sQuery(id+"F0.wireOp",EDGE,"E41")])],"isStart":true}),makeQuery(id+"F3.opExtrude","SWEPT_FACE",FACE,{"disambiguationData":[OSD([sQuery(id+"F2.wireOp",EDGE,"E42")])]})]});
            fillet(context, id + "F14", {"entities" : qUnion([Q0, Q1, Q2, Q3, Q4, Q5, Q6, Q7, Q8, Q9, Q10, Q11, Q12, Q13, Q14, Q15]), "radius" : 1 * mm, "tangentPropagation" : true, "allowEdgeOverflow" : false});
        }
    });
